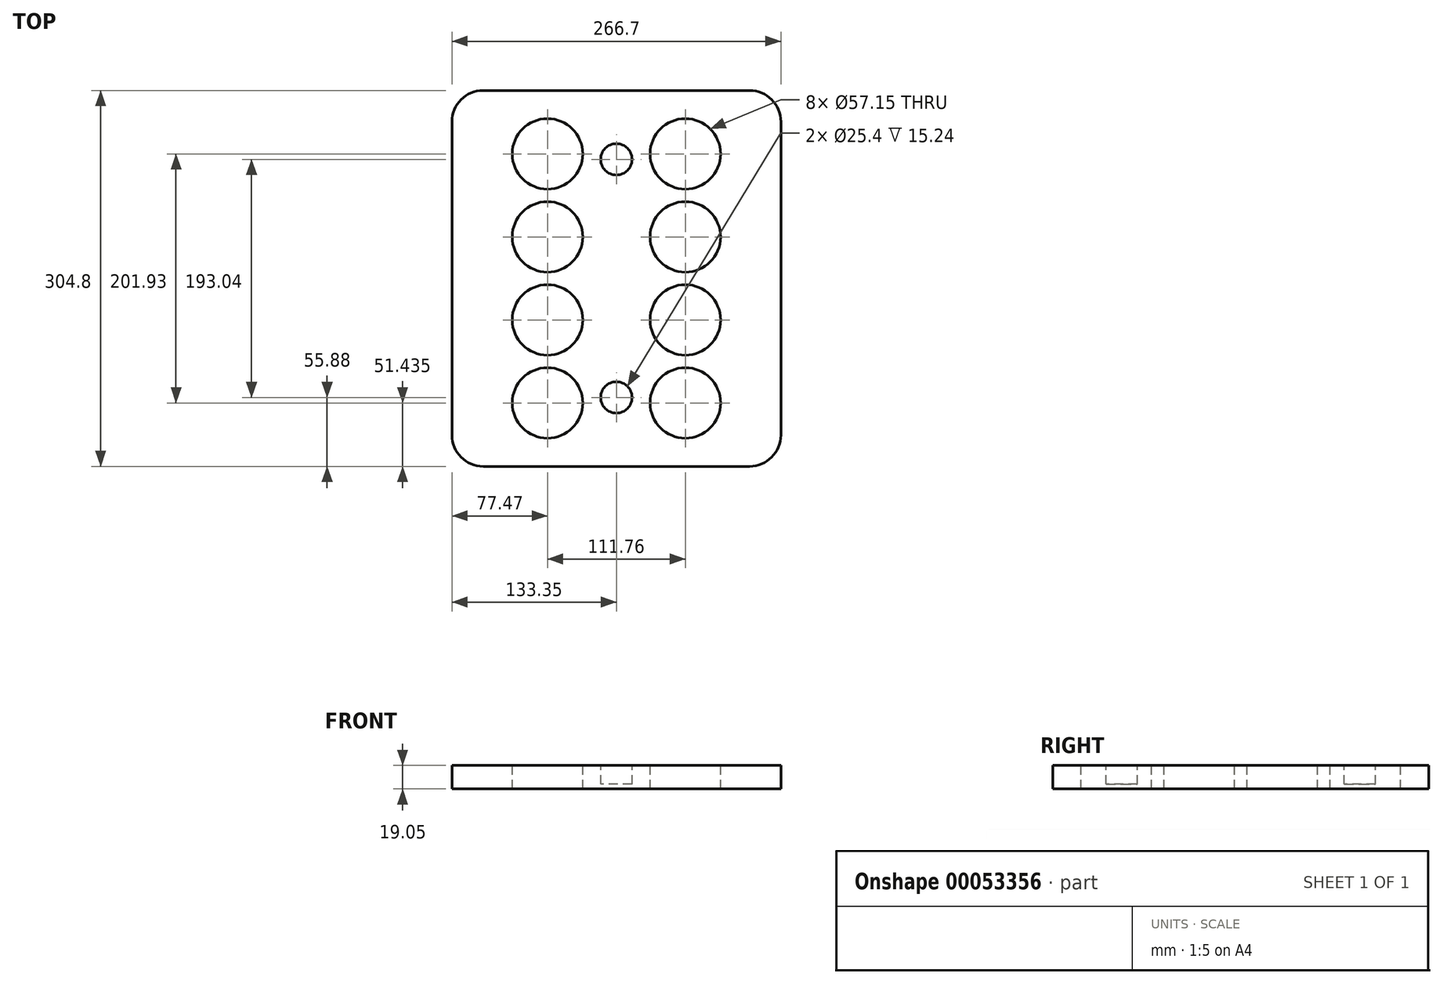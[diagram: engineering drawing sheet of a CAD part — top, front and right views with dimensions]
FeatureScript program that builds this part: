
annotation { "Feature Type Name" : "Feature", "Feature Type Description" : "" }
export const myFeature = defineFeature(function(context is Context, id is Id, definition is map)
    precondition{}
    {
        {
            var Q0;
            Q0=qCreatedBy(makeId("Top.planeOp"),FACE);
            var sketch = newSketch(context, id + "F0", { "sketchPlane" : qUnion([Q0])});
            skLineSegment(sketch, "E0.rect.bottom", {"start": v(107.95, 152.4) * mm, "end": v(-107.95, 152.4) * mm});
            skLineSegment(sketch, "E0.rect.top", {"start": v(107.95, -152.4) * mm, "end": v(-107.95, -152.4) * mm});
            skLineSegment(sketch, "E0.rect.left", {"start": v(133.35, 127) * mm, "end": v(133.35, -127) * mm});
            skLineSegment(sketch, "E0.rect.right", {"start": v(-133.35, 127) * mm, "end": v(-133.35, -127) * mm});
            skPoint(sketch, "E1.visualSharp", {"position": v(-133.35, 152.4) * mm});
            skArc(sketch, "E1.filletArc", {"start": v(-107.95, 152.4) * mm, "mid": v(-125.91, 144.96) * mm, "end": v(-133.35, 127) * mm});
            skPoint(sketch, "E2.visualSharp", {"position": v(133.35, 152.4) * mm});
            skArc(sketch, "E2.filletArc", {"start": v(133.35, 127) * mm, "mid": v(125.91, 144.96) * mm, "end": v(107.95, 152.4) * mm});
            skPoint(sketch, "E3.visualSharp", {"position": v(133.35, -152.4) * mm});
            skArc(sketch, "E3.filletArc", {"start": v(107.95, -152.4) * mm, "mid": v(125.91, -144.96) * mm, "end": v(133.35, -127) * mm});
            skPoint(sketch, "E4.visualSharp", {"position": v(-133.35, -152.4) * mm});
            skArc(sketch, "E4.filletArc", {"start": v(-133.35, -127) * mm, "mid": v(-125.91, -144.96) * mm, "end": v(-107.95, -152.4) * mm});
            skLineSegment(sketch, "E5", {"start": v(0, 170.95) * mm, "end": v(0, -181.45) * mm});
            skSolve(sketch);
        }
        {
            var Q0;
            Q0 = qSketchRegion(id + "F0", true);
            extrude(context, id + "F1", {"entities" : qUnion([Q0]), "depth" : 19.05 * mm});
        }
        {
            var Q0;
            Q0=makeQuery(id+"F1.opExtrude","CAP_FACE",FACE,{"disambiguationData":[OSD([sQuery(id+"F0.wireOp",EDGE,"E0.rect.bottom"),sQuery(id+"F0.wireOp",EDGE,"E0.rect.top"),sQuery(id+"F0.wireOp",EDGE,"E0.rect.left"),sQuery(id+"F0.wireOp",EDGE,"E0.rect.right"),sQuery(id+"F0.wireOp",EDGE,"E1.filletArc"),sQuery(id+"F0.wireOp",EDGE,"E2.filletArc"),sQuery(id+"F0.wireOp",EDGE,"E3.filletArc"),sQuery(id+"F0.wireOp",EDGE,"E4.filletArc")])],"isStart":false});
            var sketch = newSketch(context, id + "F2", { "sketchPlane" : qUnion([Q0])});
            skCircle(sketch, "E6", {"center": v(-55.88, 100.96) * mm, "radius": 28.58 * mm});
            skCircle(sketch, "E7", {"center": v(-55.88, 33.65) * mm, "radius": 28.58 * mm});
            skCircle(sketch, "E8", {"center": v(-55.88, -33.66) * mm, "radius": 28.58 * mm});
            skCircle(sketch, "E9", {"center": v(-55.88, -100.97) * mm, "radius": 28.58 * mm});
            skLineSegment(sketch, "E10", {"start": v(-211.39, 0) * mm, "end": v(197.24, 0) * mm, "construction": true});
            skPoint(sketch, "E10.endSnap0", {"position": v(-133.35, 0) * mm});
            skCircle(sketch, "E11.MirrorC", {"center": v(55.88, -100.97) * mm, "radius": 28.58 * mm});
            skCircle(sketch, "E12.MirrorC", {"center": v(55.88, -33.66) * mm, "radius": 28.58 * mm});
            skCircle(sketch, "E13.MirrorC", {"center": v(55.88, 33.65) * mm, "radius": 28.58 * mm});
            skCircle(sketch, "E14.MirrorC", {"center": v(55.88, 100.96) * mm, "radius": 28.58 * mm});
            skSolve(sketch);
        }
        {
            var Q0;
            Q0 = qSketchRegion(id + "F2", true);
            extrude(context, id + "F3", {"entities" : qUnion([Q0]), "operationType" : NewBodyOperationType.REMOVE, "endBound" : BoundingType.THROUGH_ALL, "oppositeDirection" : true, "depth" : 25.4 * mm});
        }
        {
            var Q0;
            Q0=makeQuery(id+"F1.opExtrude","CAP_FACE",FACE,{"disambiguationData":[OSD([sQuery(id+"F0.wireOp",EDGE,"E0.rect.bottom"),sQuery(id+"F0.wireOp",EDGE,"E0.rect.top"),sQuery(id+"F0.wireOp",EDGE,"E0.rect.left"),sQuery(id+"F0.wireOp",EDGE,"E0.rect.right"),sQuery(id+"F0.wireOp",EDGE,"E1.filletArc"),sQuery(id+"F0.wireOp",EDGE,"E2.filletArc"),sQuery(id+"F0.wireOp",EDGE,"E3.filletArc"),sQuery(id+"F0.wireOp",EDGE,"E4.filletArc")])],"isStart":false});
            var sketch = newSketch(context, id + "F4", { "sketchPlane" : qUnion([Q0])});
            skCircle(sketch, "E15", {"center": v(0, 96.52) * mm, "radius": 12.7 * mm});
            skCircle(sketch, "E16.MirrorC", {"center": v(0, -96.52) * mm, "radius": 12.7 * mm});
            skSolve(sketch);
        }
        {
            var Q0;
            Q0 = qSketchRegion(id + "F4", true);
            extrude(context, id + "F5", {"entities" : qUnion([Q0]), "operationType" : NewBodyOperationType.REMOVE, "oppositeDirection" : true, "depth" : 15.24 * mm});
        }
    });
